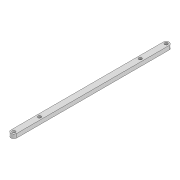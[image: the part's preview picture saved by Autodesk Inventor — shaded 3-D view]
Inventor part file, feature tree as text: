
AUTODESK INVENTOR PART (.ipt)
format: ipt  version: 2022 (Build 260153000, 153)  size: 93,696 bytes
history: native  units: mm
features: extrude x1, sketch x1
ambient origin geometry x8: Origin, YZ Plane, XZ Plane, XY Plane, X Axis, Y Axis, Z Axis, Center Point
bodies: Solid1 (feature_tree)
feature tree (2):
  extrude  "Extrusion1"  Depth=127.773mm
  sketch  "Sketch1"  dims[d0=3.2mm d1=3.2mm d2=6.0mm d3=153.89mm d6=4.0mm d7=0.0mm d10=3.2mm d11=25.907mm d12=3.2mm d13=127.773mm]
